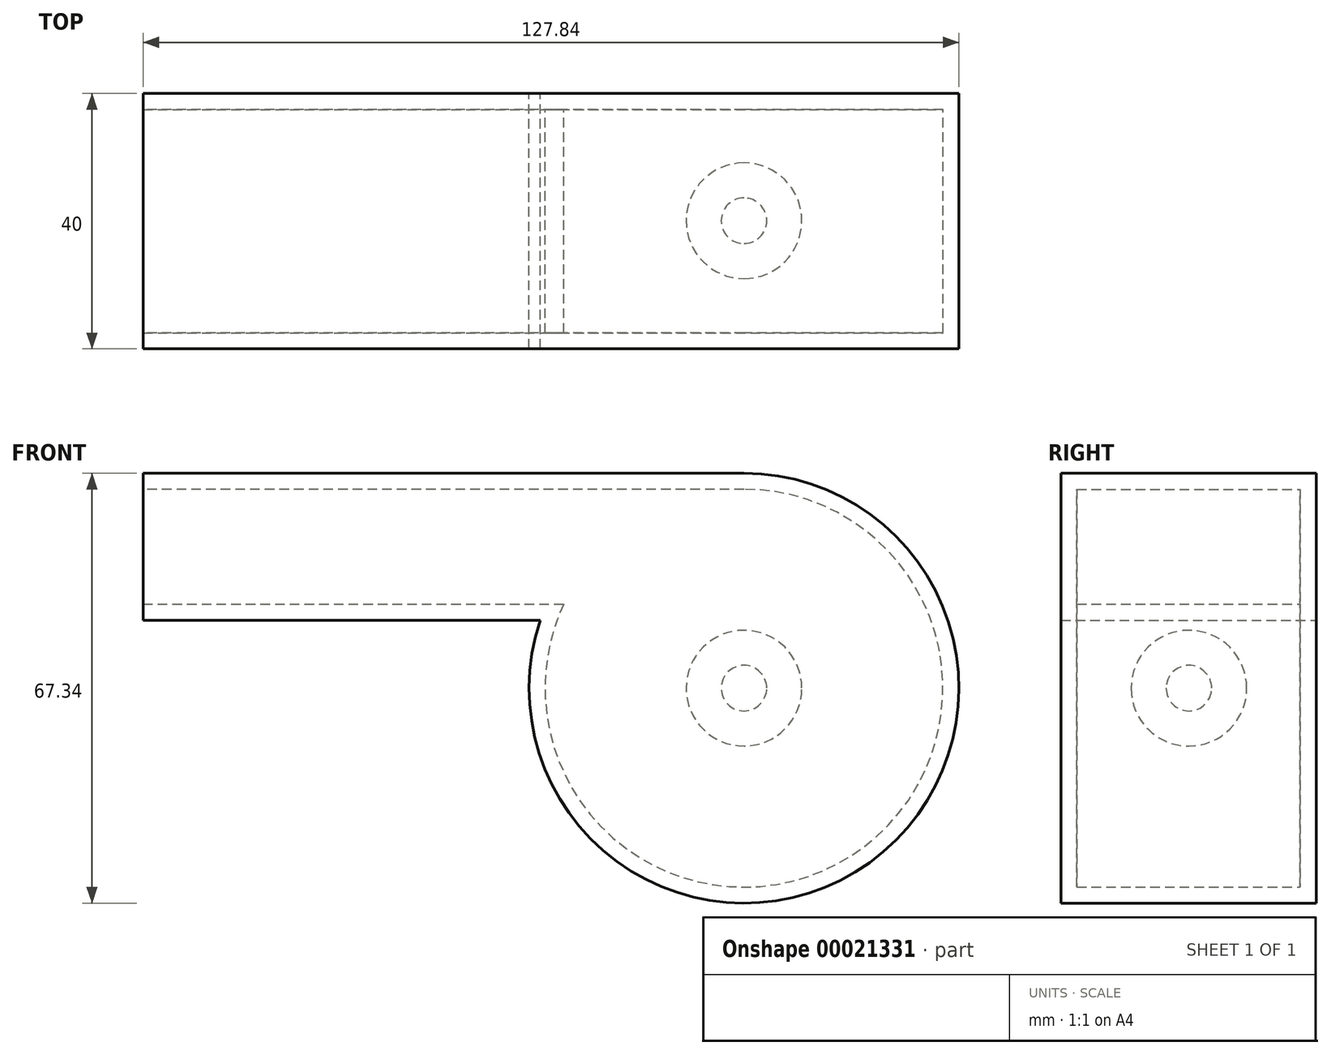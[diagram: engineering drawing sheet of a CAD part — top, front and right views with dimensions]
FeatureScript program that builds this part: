
annotation { "Feature Type Name" : "Feature", "Feature Type Description" : "" }
export const myFeature = defineFeature(function(context is Context, id is Id, definition is map)
    precondition{}
    {
        {
            var Q0;
            Q0=qCreatedBy(makeId("Front.planeOp"),FACE);
            var sketch = newSketch(context, id + "F0", { "sketchPlane" : qUnion([Q0])});
            skArc(sketch, "E0", {"start": v(-31.94, 10.64) * mm, "mid": v(19.69, -27.31) * mm, "end": v(0, 33.67) * mm});
            skLineSegment(sketch, "E1", {"start": v(0, 33.67) * mm, "end": v(-94.17, 33.67) * mm});
            skLineSegment(sketch, "E2", {"start": v(-94.17, 33.67) * mm, "end": v(-94.17, 10.64) * mm});
            skLineSegment(sketch, "E3", {"start": v(-94.17, 10.64) * mm, "end": v(-31.94, 10.64) * mm});
            skLineSegment(sketch, "E4", {"start": v(28.12, 18.52) * mm, "end": v(54.83, 48.15) * mm, "construction": true});
            skSolve(sketch);
        }
        {
            var Q0;
            Q0=makeQuery(id+"F0.imprint","IMPRINT",FACE,{"disambiguationData":[TD([[makeQuery(id+"F0.imprint","IMPRINT",EDGE,{"derivedFrom":sQuery(id+"F0.wireOp",EDGE,"E0")}),1.0]])]});
            extrude(context, id + "F1", {"entities" : qUnion([Q0]), "depth" : 40 * mm});
        }
        {
            var Q0;
            Q0=makeQuery(id+"F1.opExtrude","SWEPT_FACE",FACE,{"disambiguationData":[OSD([sQuery(id+"F0.wireOp",EDGE,"E2")])]});
            shell(context, id + "F2", {"entities" : qUnion([Q0]), "thickness" : 2.5 * mm});
        }
        {
            var Q0;
            Q0=qCreatedBy(makeId("Top.planeOp"),FACE);
            var sketch = newSketch(context, id + "F3", { "sketchPlane" : qUnion([Q0])});
            skArc(sketch, "E5", {"start": v(0, -29) * mm, "mid": v(9.07, -19.94) * mm, "end": v(0, -10.88) * mm});
            skLineSegment(sketch, "E6", {"start": v(0, -10.88) * mm, "end": v(0, -16.37) * mm});
            skArc(sketch, "E7", {"start": v(0, -23.51) * mm, "mid": v(3.57, -19.94) * mm, "end": v(0, -16.37) * mm});
            skLineSegment(sketch, "E8.trimOffspring", {"start": v(0, -23.51) * mm, "end": v(0, -29) * mm});
            skLineSegment(sketch, "E9", {"start": v(0, -29) * mm, "end": v(0, -35.35) * mm, "construction": true});
            skSolve(sketch);
        }
        {
            var Q0;
            Q0=makeQuery(id+"F3.imprint","IMPRINT",FACE,{"disambiguationData":[TD([[makeQuery(id+"F3.imprint","IMPRINT",EDGE,{"derivedFrom":sQuery(id+"F3.wireOp",EDGE,"E5")}),1.0]])]});
            var Q1;
            Q1=sQuery(id+"F3.wireOp",EDGE,"E9");
            revolve(context, id + "F4", {"entities" : qUnion([Q0]), "axis" : qUnion([Q1]), "revolveType" : RevolveType.FULL});
        }
        {
            var Q0;
            Q0=makeQuery(id+"F1.opExtrude","CAP_FACE",FACE,{"disambiguationData":[OSD([sQuery(id+"F0.wireOp",EDGE,"E0"),sQuery(id+"F0.wireOp",EDGE,"E1"),sQuery(id+"F0.wireOp",EDGE,"E2"),sQuery(id+"F0.wireOp",EDGE,"E3")])],"isStart":false});
            var sketch = newSketch(context, id + "F5", { "sketchPlane" : qUnion([Q0])});
            skLineSegment(sketch, "E10.0", {"start": v(28.12, 18.52) * mm, "end": v(54.83, 48.15) * mm});
            skSolve(sketch);
        }
        {
            var Q0;
            Q0=sQuery(id+"F0.wireOp",VERTEX,"86d5cee2-a577-4ad6-9f4f-85df5e04b25c.end");
            var Q1;
            Q1=sQuery(id+"F0.wireOp",VERTEX,"86d5cee2-a577-4ad6-9f4f-85df5e04b25c.start");
            var Q2;
            Q2=sQuery(id+"F5.wireOp",VERTEX,"d996dbe9-9980-4e05-a296-ce69eedc65b2.0.start");
            var Q3;
            Q3=sQuery(id+"F5.wireOp",VERTEX,"E10.0.end");
            var Q4;
            Q4=sQuery(id+"F0.wireOp",VERTEX,"E4.end");
            var Q5;
            Q5=sQuery(id+"F0.wireOp",VERTEX,"E4.start");
            cPlane(context, id + "F6", {"entities" : qUnion([Q0, Q1, Q2, Q3, Q4, Q5]), "cplaneType" : CPlaneType.THREE_POINT, "offset" : 150 * mm, "width" : 150 * mm, "height" : 150 * mm});
        }
    });
